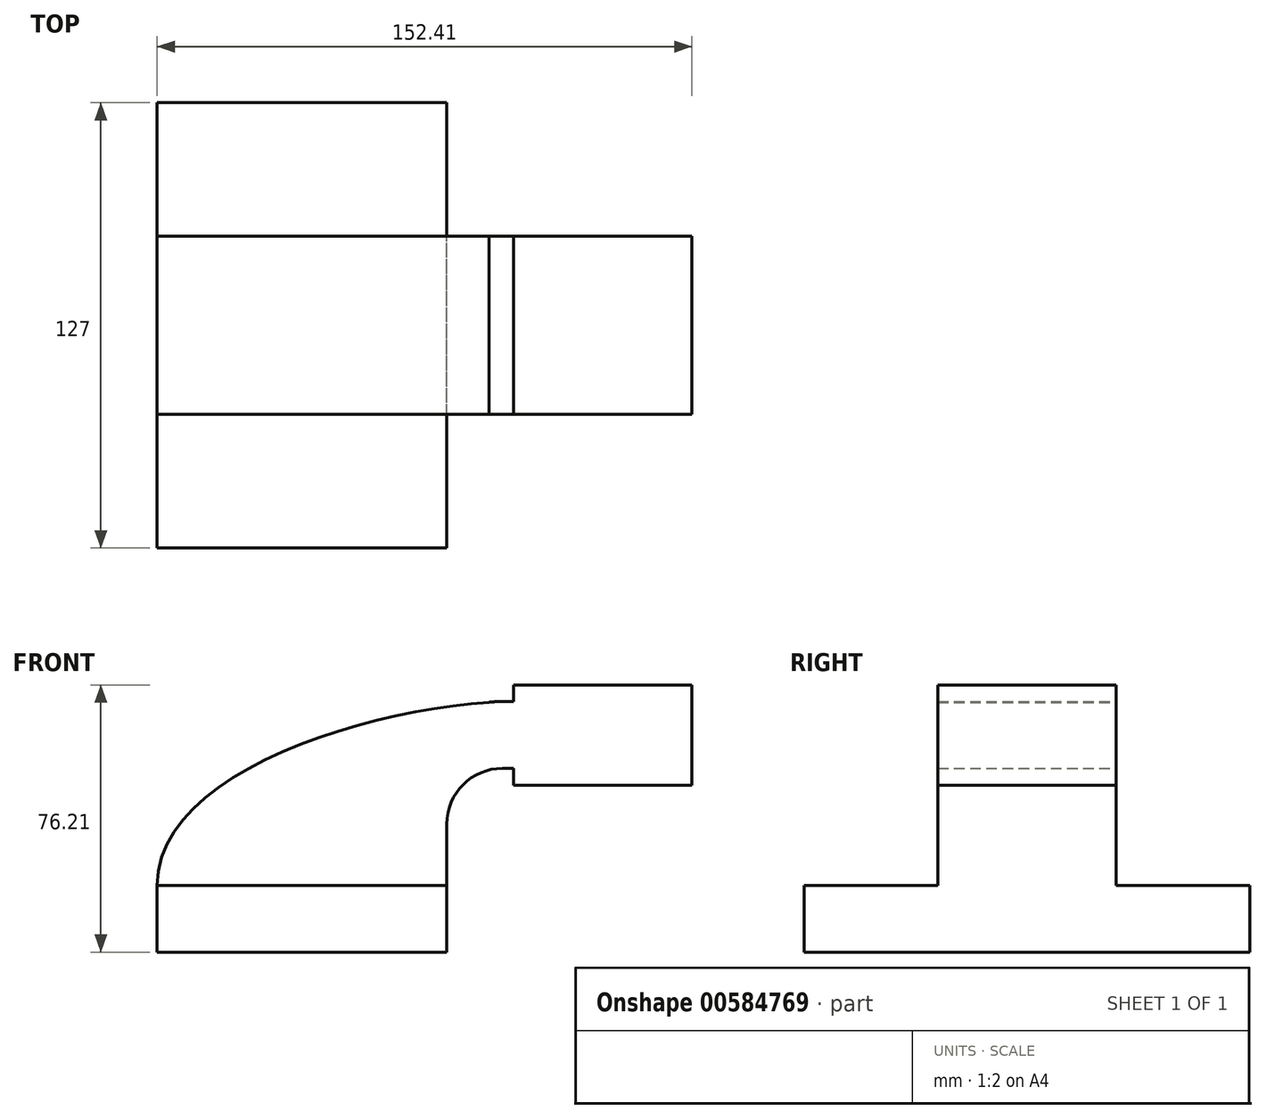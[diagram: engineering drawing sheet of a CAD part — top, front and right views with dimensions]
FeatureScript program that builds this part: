
annotation { "Feature Type Name" : "Feature", "Feature Type Description" : "" }
export const myFeature = defineFeature(function(context is Context, id is Id, definition is map)
    precondition{}
    {
        {
            var Q0;
            Q0=qCreatedBy(makeId("Front.planeOp"),FACE);
            var sketch = newSketch(context, id + "F0", { "sketchPlane" : qUnion([Q0])});
            skLineSegment(sketch, "E0.bottom", {"start": v(-41.28, 9.52) * mm, "end": v(41.28, 9.53) * mm});
            skLineSegment(sketch, "E0.top", {"start": v(-41.28, -9.53) * mm, "end": v(41.28, -9.53) * mm});
            skLineSegment(sketch, "E0.left", {"start": v(-41.28, 9.52) * mm, "end": v(-41.28, -9.53) * mm});
            skLineSegment(sketch, "E0.right", {"start": v(41.28, 9.53) * mm, "end": v(41.28, -9.52) * mm});
            skPoint(sketch, "E0.middle", {"position": v(0, 0) * mm});
            skLineSegment(sketch, "E1.bottom", {"start": v(60.33, 38.1) * mm, "end": v(111.12, 38.1) * mm});
            skLineSegment(sketch, "E1.top", {"start": v(60.33, 66.68) * mm, "end": v(111.12, 66.68) * mm});
            skLineSegment(sketch, "E1.left", {"start": v(60.33, 38.1) * mm, "end": v(60.32, 66.68) * mm});
            skLineSegment(sketch, "E1.right", {"start": v(111.12, 38.1) * mm, "end": v(111.12, 66.68) * mm});
            skPoint(sketch, "E1.middle", {"position": v(85.72, 52.39) * mm});
            skLineSegment(sketch, "E2", {"start": v(41.27, 9.53) * mm, "end": v(41.27, 27) * mm});
            skArc(sketch, "E3", {"start": v(41.27, 27) * mm, "mid": v(45.92, 38.23) * mm, "end": v(57.15, 42.88) * mm});
            skLineSegment(sketch, "E4", {"start": v(57.15, 42.88) * mm, "end": v(85.72, 42.88) * mm});
            skPoint(sketch, "E5", {"position": v(85.72, 38.1) * mm});
            skLineSegment(sketch, "E6.0", {"start": v(57.15, 61.93) * mm, "end": v(85.72, 61.93) * mm});
            skArc(sketch, "E6.1", {"start": v(22.22, 27) * mm, "mid": v(32.45, 51.7) * mm, "end": v(57.15, 61.93) * mm});
            skLineSegment(sketch, "E6.2", {"start": v(22.22, 9.53) * mm, "end": v(22.22, 27) * mm});
            skFitSpline(sketch, "E7", {"points": [v(-41.28, 9.52) * mm, v(57.15, 61.93) * mm], "startDerivative": vector(0.03, 97.6) * mm, "endDerivative": vector(111.88, 4.7) * mm});
            skSolve(sketch);
        }
        {
            var Q0;
            Q0=makeQuery(id+"F0.imprint","IMPRINT",FACE,{"disambiguationData":[TD([[makeQuery(id+"F0.imprint","IMPRINT",EDGE,{"derivedFrom":sQuery(id+"F0.wireOp",EDGE,"E0.top")}),1.0]])]});
            extrude(context, id + "F1", {"entities" : qUnion([Q0]), "endBound" : BoundingType.SYMMETRIC, "depth" : 127 * mm, "offsetDistance" : 25.4 * mm});
        }
        {
            var Q0;
            Q0 = qSketchRegion(id + "F0", true);
            extrude(context, id + "F2", {"entities" : qUnion([Q0]), "operationType" : NewBodyOperationType.ADD, "endBound" : BoundingType.SYMMETRIC, "depth" : 50.8 * mm, "offsetDistance" : 25.4 * mm});
        }
    });
